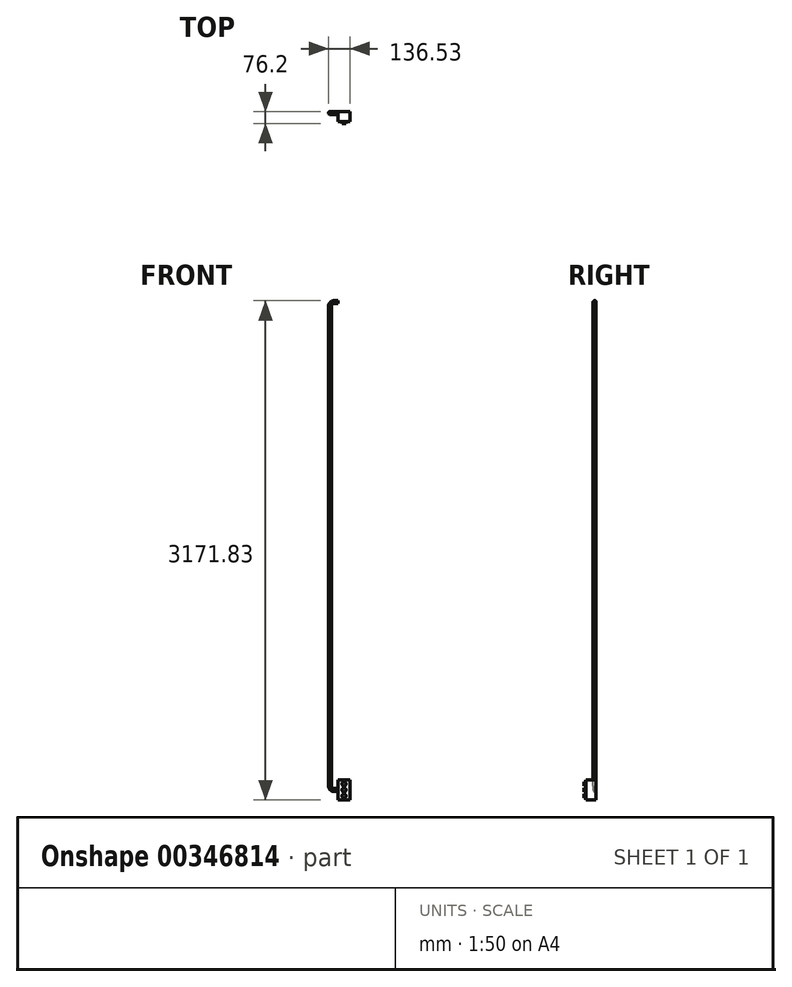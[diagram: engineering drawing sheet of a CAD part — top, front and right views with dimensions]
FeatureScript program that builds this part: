
annotation { "Feature Type Name" : "Feature", "Feature Type Description" : "" }
export const myFeature = defineFeature(function(context is Context, id is Id, definition is map)
    precondition{}
    {
        {
            var Q0;
            Q0=qCreatedBy(makeId("Front.planeOp"),FACE);
            var sketch = newSketch(context, id + "F0", { "sketchPlane" : qUnion([Q0])});
            skLineSegment(sketch, "E0.bottom", {"start": v(0, 0) * mm, "end": v(76.2, 0) * mm});
            skLineSegment(sketch, "E0.top", {"start": v(0, 127) * mm, "end": v(76.2, 127) * mm});
            skLineSegment(sketch, "E0.left", {"start": v(0, 0) * mm, "end": v(0, 127) * mm});
            skLineSegment(sketch, "E0.right", {"start": v(76.2, 0) * mm, "end": v(76.2, 127) * mm});
            skSolve(sketch);
        }
        {
            var Q0;
            Q0=makeQuery(id+"F0.imprint","IMPRINT",FACE,{"disambiguationData":[TD([[makeQuery(id+"F0.imprint","IMPRINT",EDGE,{"derivedFrom":sQuery(id+"F0.wireOp",EDGE,"E0.bottom")}),1.0]])]});
            extrude(context, id + "F1", {"entities" : qUnion([Q0]), "depth" : 63.5 * mm});
        }
        {
            var Q0;
            Q0=makeQuery(id+"F1.opExtrude","CAP_FACE",FACE,{"disambiguationData":[OSD([sQuery(id+"F0.wireOp",EDGE,"E0.bottom"),sQuery(id+"F0.wireOp",EDGE,"E0.top"),sQuery(id+"F0.wireOp",EDGE,"E0.left"),sQuery(id+"F0.wireOp",EDGE,"E0.right")])],"isStart":false});
            var sketch = newSketch(context, id + "F2", { "sketchPlane" : qUnion([Q0])});
            skCircle(sketch, "E1", {"center": v(38.1, 25.4) * mm, "radius": 12.7 * mm});
            skCircle(sketch, "E2", {"center": v(38.1, 101.6) * mm, "radius": 12.7 * mm});
            skCircle(sketch, "E3", {"center": v(38.1, 63.5) * mm, "radius": 12.7 * mm});
            skSolve(sketch);
        }
        {
            var Q0;
            Q0 = qSketchRegion(id + "F2", true);
            extrude(context, id + "F3", {"entities" : qUnion([Q0]), "operationType" : NewBodyOperationType.ADD, "depth" : 12.7 * mm});
        }
        {
            var Q0;
            Q0=qCreatedBy(makeId("Front.planeOp"),FACE);
            cPlane(context, id + "F4", {"entities" : qUnion([Q0]), "cplaneType" : CPlaneType.OFFSET, "offset" : 9.52 * mm, "width" : 152.4 * mm, "height" : 152.4 * mm});
        }
        {
            var Q0;
            Q0=qCreatedBy(id+"F4.planeOp",FACE);
            var sketch = newSketch(context, id + "F5", { "sketchPlane" : qUnion([Q0])});
            skLineSegment(sketch, "E4", {"start": v(0, 63.5) * mm, "end": v(-25.4, 63.5) * mm});
            skArc(sketch, "E5", {"start": v(-50.8, 88.9) * mm, "mid": v(-43.36, 70.94) * mm, "end": v(-25.4, 63.5) * mm});
            skLineSegment(sketch, "E6", {"start": v(-50.8, 88.9) * mm, "end": v(-50.8, 3136.9) * mm});
            skArc(sketch, "E7", {"start": v(-25.4, 3162.3) * mm, "mid": v(-43.36, 3154.86) * mm, "end": v(-50.8, 3136.9) * mm});
            skLineSegment(sketch, "E8", {"start": v(-25.4, 3162.3) * mm, "end": v(0, 3162.3) * mm});
            skSolve(sketch);
        }
        {
            var Q0;
            Q0=makeQuery(id+"F1.opExtrude","SWEPT_FACE",FACE,{"disambiguationData":[OSD([sQuery(id+"F0.wireOp",EDGE,"E0.left")])]});
            var sketch = newSketch(context, id + "F6", { "sketchPlane" : qUnion([Q0])});
            skCircle(sketch, "E9", {"center": v(9.53, 63.5) * mm, "radius": 9.53 * mm});
            skSolve(sketch);
        }
        {
            var Q0;
            Q0=makeQuery(id+"F6.imprint","IMPRINT",FACE,{"disambiguationData":[TD([[makeQuery(id+"F6.imprint","IMPRINT",EDGE,{"derivedFrom":sQuery(id+"F6.wireOp",EDGE,"E9")}),1.0]])]});
            var Q1;
            Q1=sQuery(id+"F5.wireOp",EDGE,"E4");
            var Q2;
            Q2=sQuery(id+"F5.wireOp",EDGE,"E5");
            var Q3;
            Q3=sQuery(id+"F5.wireOp",EDGE,"E6");
            var Q4;
            Q4=sQuery(id+"F5.wireOp",EDGE,"E7");
            var Q5;
            Q5=sQuery(id+"F5.wireOp",EDGE,"E8");
            sweep(context, id + "F7", {"operationType" : NewBodyOperationType.ADD, "profiles" : qUnion([Q0]), "path" : qUnion([Q1, Q2, Q3, Q4, Q5])});
        }
    });
